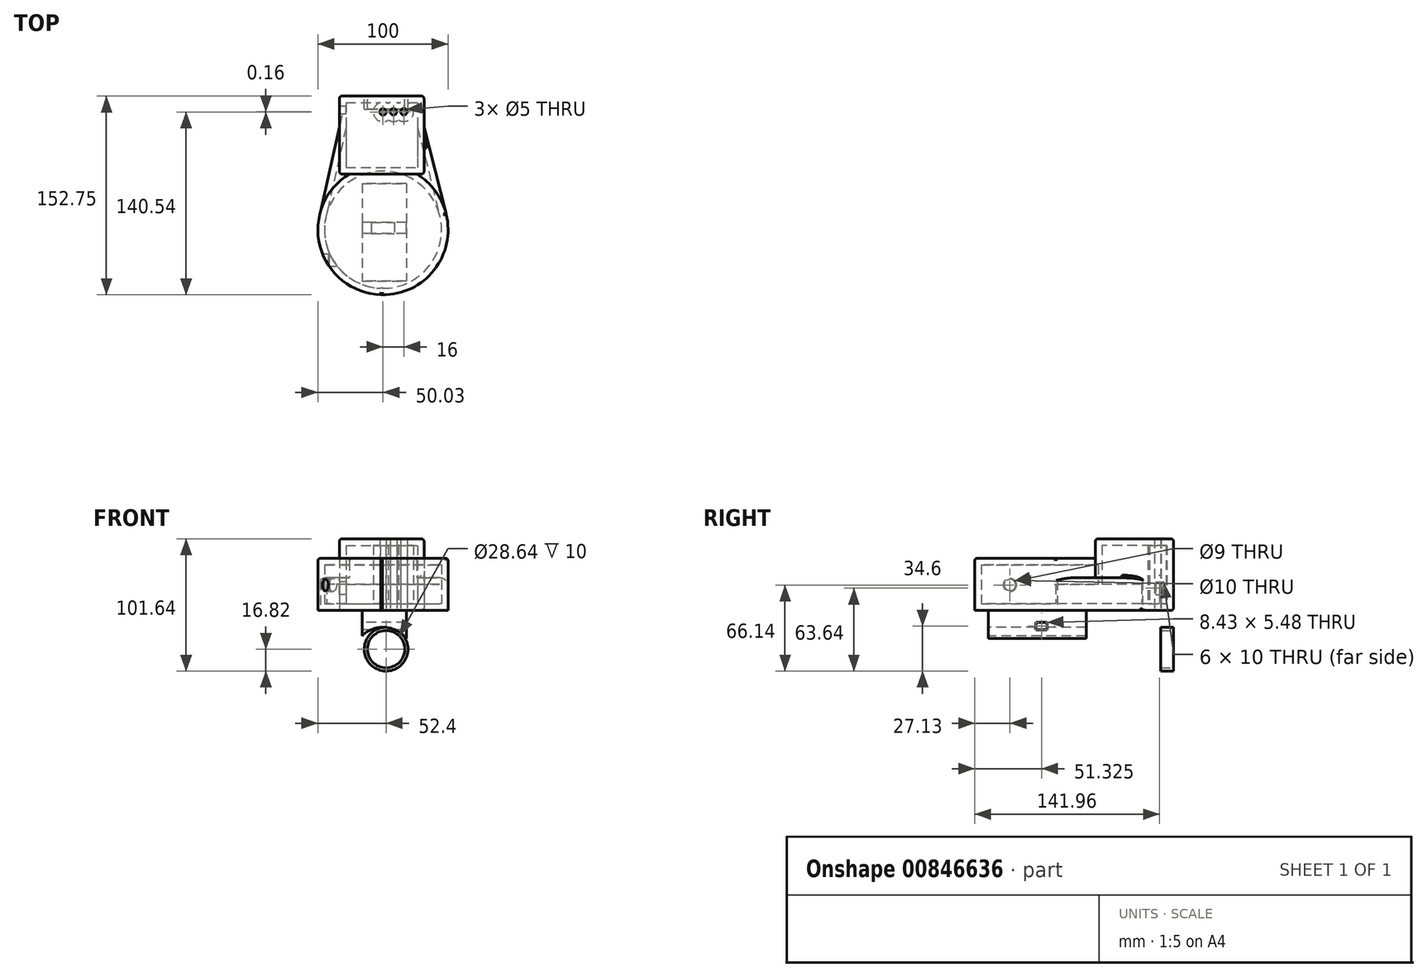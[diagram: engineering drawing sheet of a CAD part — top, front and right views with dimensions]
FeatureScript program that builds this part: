
annotation { "Feature Type Name" : "Feature", "Feature Type Description" : "" }
export const myFeature = defineFeature(function(context is Context, id is Id, definition is map)
    precondition{}
    {
        {
            var Q0;
            Q0=qCreatedBy(makeId("Top.planeOp"),FACE);
            var sketch = newSketch(context, id + "F0", { "sketchPlane" : qUnion([Q0])});
            skLineSegment(sketch, "E0.bottom", {"start": v(-33.47, 67.15) * mm, "end": v(31.53, 67.15) * mm});
            skLineSegment(sketch, "E0.top", {"start": v(-33.47, 7.15) * mm, "end": v(31.53, 7.15) * mm});
            skLineSegment(sketch, "E0.left", {"start": v(-33.47, 67.15) * mm, "end": v(-33.47, 7.15) * mm});
            skLineSegment(sketch, "E0.right", {"start": v(31.53, 67.15) * mm, "end": v(31.53, 7.15) * mm});
            skLineSegment(sketch, "E1.top", {"start": v(-28.47, 32.15) * mm, "end": v(-23.47, 32.15) * mm});
            skLineSegment(sketch, "E1.left", {"start": v(-28.47, 42.15) * mm, "end": v(-28.47, 32.15) * mm});
            skLineSegment(sketch, "E1.right", {"start": v(-23.47, 42.15) * mm, "end": v(-23.47, 32.15) * mm});
            skCircle(sketch, "E2", {"center": v(0, -35.6) * mm, "radius": 50 * mm});
            skLineSegment(sketch, "E3", {"start": v(-28.47, 42.15) * mm, "end": v(-23.47, 42.15) * mm});
            skCircle(sketch, "E4", {"center": v(0.03, 54.94) * mm, "radius": 2.5 * mm});
            skCircle(sketch, "E5", {"center": v(8.03, 55.08) * mm, "radius": 2.5 * mm});
            skCircle(sketch, "E6", {"center": v(16.03, 55.1) * mm, "radius": 2.5 * mm});
            skPoint(sketch, "E7.endSnap0", {"position": v(63.48, -66.15) * mm});
            skPoint(sketch, "E7.start.orphan", {"position": v(90.68, -62.3) * mm});
            skPoint(sketch, "E8.start.orphan", {"position": v(63.48, -90.93) * mm});
            skLineSegment(sketch, "E9", {"start": v(-33.47, 7.15) * mm, "end": v(-33.47, 1.55) * mm});
            skLineSegment(sketch, "E10", {"start": v(31.53, 7.15) * mm, "end": v(32.4, 2.49) * mm});
            skPoint(sketch, "E11.end.orphan", {"position": v(36.27, -70.01) * mm});
            skLineSegment(sketch, "E12", {"start": v(31.53, 43.32) * mm, "end": v(50.78, -32.42) * mm});
            skLineSegment(sketch, "E13", {"start": v(-33.47, 43.32) * mm, "end": v(-48.16, -22.17) * mm});
            skLineSegment(sketch, "E14", {"start": v(46.54, -86.53) * mm, "end": v(-67.67, -84.26) * mm});
            skSolve(sketch);
        }
        {
            var Q0;
            {var subQ1=sQuery(id+"F0.wireOp",EDGE,"E2");var subQ8=makeQuery(id+"F0.imprint","INTERSECT",VERTEX,{"derivedFrom":[subQ1,sQuery(id+"F0.wireOp",EDGE,"E10")]});Q0=makeQuery(id+"F0.imprint","IMPRINT",FACE,{"disambiguationData":[TD([[makeQuery(id+"F0.imprint","IMPRINT",EDGE,{"disambiguationData":[TD([[subQ8,1.0]])],"derivedFrom":subQ1}),1.0]])]});}
            var Q1;
            Q1=sQuery(id+"F0.wireOp",EDGE,"E2");
            extrude(context, id + "F1", {"entities" : qUnion([Q0]), "surfaceEntities" : qUnion([Q1]), "depth" : 40 * mm, "offsetDistance" : 25 * mm});
        }
        {
            var Q0;
            {var subQ0=sQuery(id+"F0.wireOp",EDGE,"E9");Q0=makeQuery(id+"F0.imprint","IMPRINT",FACE,{"disambiguationData":[TD([[makeQuery(id+"F0.imprint","IMPRINT",EDGE,{"derivedFrom":subQ0}),-1.0]])]});}
            var Q1;
            Q1=makeQuery(id+"F0.imprint","IMPRINT",FACE,{"disambiguationData":[TD([[makeQuery(id+"F0.imprint","IMPRINT",EDGE,{"derivedFrom":sQuery(id+"F0.wireOp",EDGE,"E0.top")}),-1.0]])]});
            var Q2;
            {var subQ0=sQuery(id+"F0.wireOp",EDGE,"E10");Q2=makeQuery(id+"F0.imprint","IMPRINT",FACE,{"disambiguationData":[TD([[makeQuery(id+"F0.imprint","IMPRINT",EDGE,{"derivedFrom":subQ0}),1.0]])]});}
            extrude(context, id + "F2", {"entities" : qUnion([Q0, Q1, Q2]), "operationType" : NewBodyOperationType.ADD, "depth" : 25 * mm, "offsetDistance" : 25 * mm});
        }
        {
            var Q0;
            Q0=makeQuery(id+"F0.imprint","IMPRINT",FACE,{"disambiguationData":[TD([[makeQuery(id+"F0.imprint","IMPRINT",EDGE,{"derivedFrom":sQuery(id+"F0.wireOp",EDGE,"E1.top")}),1.0]])]});
            var Q1;
            {var subQ3=sQuery(id+"F0.wireOp",EDGE,"E0.bottom");Q1=makeQuery(id+"F0.imprint","IMPRINT",FACE,{"disambiguationData":[TD([[makeQuery(id+"F0.imprint","IMPRINT",EDGE,{"derivedFrom":subQ3}),-1.0]])]});}
            var Q2;
            Q2=makeQuery(id+"F0.imprint","IMPRINT",FACE,{"disambiguationData":[TD([[makeQuery(id+"F0.imprint","IMPRINT",EDGE,{"derivedFrom":sQuery(id+"F0.wireOp",EDGE,"E4")}),1.0]])]});
            var Q3;
            Q3=makeQuery(id+"F0.imprint","IMPRINT",FACE,{"disambiguationData":[TD([[makeQuery(id+"F0.imprint","IMPRINT",EDGE,{"derivedFrom":sQuery(id+"F0.wireOp",EDGE,"E5")}),1.0]])]});
            var Q4;
            Q4=makeQuery(id+"F0.imprint","IMPRINT",FACE,{"disambiguationData":[TD([[makeQuery(id+"F0.imprint","IMPRINT",EDGE,{"derivedFrom":sQuery(id+"F0.wireOp",EDGE,"E6")}),1.0]])]});
            var Q5;
            {var subQ0=sQuery(id+"F0.wireOp",EDGE,"E2");var subQ1=sQuery(id+"F0.wireOp",EDGE,"E0.top");var subQ2=makeQuery(id+"F0.imprint","INTERSECT",VERTEX,{"disambiguationData":[OD(0.0)],"derivedFrom":[subQ1,subQ0]});Q5=makeQuery(id+"F0.imprint","IMPRINT",FACE,{"disambiguationData":[TD([[makeQuery(id+"F0.imprint","IMPRINT",EDGE,{"disambiguationData":[TD([[subQ2,-1.0]])],"derivedFrom":subQ1}),1.0]])]});}
            extrude(context, id + "F3", {"entities" : qUnion([Q0, Q1, Q2, Q3, Q4, Q5]), "operationType" : NewBodyOperationType.ADD, "surfaceOperationType" : NewSurfaceOperationType.ADD, "depth" : 55 * mm, "offsetDistance" : 25 * mm});
        }
        {
            var Q0;
            Q0=makeQuery(id+"F3.opExtrude","SWEPT_FACE",FACE,{"disambiguationData":[OSD([sQuery(id+"F0.wireOp",EDGE,"E0.bottom")])]});
            var sketch = newSketch(context, id + "F4", { "sketchPlane" : qUnion([Q0])});
            skCircle(sketch, "E15", {"center": v(-2.4, -29.82) * mm, "radius": 14.32 * mm});
            skCircle(sketch, "E16", {"center": v(-2.4, -29.82) * mm, "radius": 16.82 * mm});
            skLineSegment(sketch, "E17", {"start": v(-9.01, 0) * mm, "end": v(-9.01, -14.35) * mm});
            skLineSegment(sketch, "E18", {"start": v(4.98, 0) * mm, "end": v(4.98, -14.7) * mm});
            skSolve(sketch);
        }
        {
            var Q0;
            Q0=sQuery(id+"F0.wireOp",VERTEX,"E4.center");
            var Q1;
            Q1=sQuery(id+"F0.wireOp",VERTEX,"E5.center");
            var Q2;
            Q2=sQuery(id+"F0.wireOp",VERTEX,"E6.center");
            var Q3;
            Q3=makeQuery(id+"F1.opExtrude","SWEPT_BODY",BODY,{"disambiguationData":[OSD([sQuery(id+"F0.wireOp",EDGE,"E2"),sQuery(id+"F0.wireOp",EDGE,"5vXzBK3q-LOnD-Q0HQ-j5aD-O0o9f5yey0at"),sQuery(id+"F0.wireOp",EDGE,"E11")])]});
            hole(context, id + "F5", {"style" : HoleStyle.SIMPLE, "endStyle" : HoleEndStyle.THROUGH, "oppositeDirection" : true, "holeDiameter" : 5 * mm, "majorDiameter" : 5 * mm, "isTappedThrough" : true, "tappedDepth" : 12 * mm, "tapClearance" : 3, "locations" : qUnion([Q0, Q1, Q2]), "scope" : qUnion([Q3])});
        }
        {
            var Q0;
            Q0=makeQuery(id+"F3.opExtrude","SWEPT_FACE",FACE,{"disambiguationData":[OSD([sQuery(id+"F0.wireOp",EDGE,"E0.left")])]});
            var sketch = newSketch(context, id + "F6", { "sketchPlane" : qUnion([Q0])});
            skLineSegment(sketch, "E19.bottom", {"start": v(-59.36, 12) * mm, "end": v(-53.36, 12) * mm});
            skLineSegment(sketch, "E19.top", {"start": v(-59.36, 22) * mm, "end": v(-53.36, 22) * mm});
            skLineSegment(sketch, "E19.left", {"start": v(-59.36, 12) * mm, "end": v(-59.36, 22) * mm});
            skLineSegment(sketch, "E19.right", {"start": v(-53.36, 12) * mm, "end": v(-53.36, 22) * mm});
            skCircle(sketch, "E20", {"center": v(58.47, 19.5) * mm, "radius": 4.5 * mm});
            skSolve(sketch);
        }
        {
            var Q0;
            {var subQ0=sQuery(id+"F4.wireOp",EDGE,"E17");Q0=makeQuery(id+"F4.imprint","IMPRINT",FACE,{"disambiguationData":[TD([[makeQuery(id+"F4.imprint","IMPRINT",EDGE,{"derivedFrom":subQ0}),1.0]])]});}
            var Q1;
            Q1=makeQuery(id+"F4.imprint","IMPRINT",FACE,{"disambiguationData":[TD([[makeQuery(id+"F4.imprint","IMPRINT",EDGE,{"derivedFrom":sQuery(id+"F4.wireOp",EDGE,"E15")}),-1.0]])]});
            extrude(context, id + "F7", {"entities" : qUnion([Q0, Q1]), "operationType" : NewBodyOperationType.ADD, "oppositeDirection" : true, "depth" : 10 * mm, "offsetDistance" : 25 * mm});
        }
        {
            var Q0;
            Q0=makeQuery(id+"F1.opExtrude","SWEPT_FACE",FACE,{"disambiguationData":[OSD([sQuery(id+"F0.wireOp",EDGE,"E2")])]});
            var Q1;
            Q1=makeQuery(id+"F2.opExtrude","SWEPT_FACE",FACE,{"disambiguationData":[OSD([sQuery(id+"F0.wireOp",EDGE,"E12")])]});
            var Q2;
            {var subQ0=sQuery(id+"F0.wireOp",EDGE,"E0.right");var subQ1=sQuery(id+"F0.wireOp",EDGE,"E0.left");var subQ2=sQuery(id+"F0.wireOp",EDGE,"E0.top");var subQ3=sQuery(id+"F0.wireOp",EDGE,"E2");Q2=makeQuery(id+"F3.boolean.opBoolean","MERGE",FACE,{"derivedFrom":[makeQuery(id+"F2.boolean.opBoolean","MERGE",FACE,{"derivedFrom":[makeQuery(id+"F1.opExtrude","CAP_FACE",FACE,{"disambiguationData":[OSD([subQ2,subQ3])],"isStart":true}),makeQuery(id+"F2.opExtrude","CAP_FACE",FACE,{"disambiguationData":[OSD([subQ2,subQ1,subQ3,sQuery(id+"F0.wireOp",EDGE,"E13")])],"isStart":true}),makeQuery(id+"F2.opExtrude","CAP_FACE",FACE,{"disambiguationData":[OSD([subQ2,subQ0,subQ3,sQuery(id+"F0.wireOp",EDGE,"E12")])],"isStart":true})]}),makeQuery(id+"F3.opExtrude","CAP_FACE",FACE,{"disambiguationData":[OSD([sQuery(id+"F0.wireOp",EDGE,"E0.bottom"),subQ2,subQ1,subQ0])],"isStart":true})]});}
            var Q3;
            Q3=makeQuery(id+"F3.opExtrude","SWEPT_FACE",FACE,{"disambiguationData":[OSD([sQuery(id+"F0.wireOp",EDGE,"E0.right")])]});
            var Q4;
            Q4=makeQuery(id+"F3.opExtrude","SWEPT_FACE",FACE,{"disambiguationData":[OSD([sQuery(id+"F0.wireOp",EDGE,"E0.left")])]});
            var Q5;
            Q5=makeQuery(id+"F3.opExtrude","CAP_FACE",FACE,{"disambiguationData":[OSD([sQuery(id+"F0.wireOp",EDGE,"E0.bottom"),sQuery(id+"F0.wireOp",EDGE,"E0.top"),sQuery(id+"F0.wireOp",EDGE,"E0.left"),sQuery(id+"F0.wireOp",EDGE,"E0.right")])],"isStart":false});
            var Q6;
            Q6=makeQuery(id+"F3.opExtrude","SWEPT_FACE",FACE,{"disambiguationData":[OSD([sQuery(id+"F0.wireOp",EDGE,"E0.top")])]});
            var Q7;
            Q7=makeQuery(id+"F2.opExtrude","CAP_FACE",FACE,{"disambiguationData":[OSD([sQuery(id+"F0.wireOp",EDGE,"E0.top"),sQuery(id+"F0.wireOp",EDGE,"E0.left"),sQuery(id+"F0.wireOp",EDGE,"E2"),sQuery(id+"F0.wireOp",EDGE,"E13")])],"isStart":false});
            var Q8;
            Q8=makeQuery(id+"F1.opExtrude","SWEPT_BODY",BODY,{"disambiguationData":[OSD([sQuery(id+"F0.wireOp",EDGE,"E0.top"),sQuery(id+"F0.wireOp",EDGE,"E2")])]});
            shell(context, id + "F8", {"isHollow" : true, "entities" : qUnion([Q0, Q1, Q2, Q3, Q4, Q5, Q6, Q7]), "parts" : qUnion([Q8]), "thickness" : 5 * mm});
        }
        {
            var Q0;
            Q0=sQuery(id+"F6.wireOp",VERTEX,"E20.center");
            var Q1;
            Q1=makeQuery(id+"F1.opExtrude","SWEPT_BODY",BODY,{"disambiguationData":[OSD([sQuery(id+"F0.wireOp",EDGE,"E0.top"),sQuery(id+"F0.wireOp",EDGE,"E2")])]});
            hole(context, id + "F9", {"style" : HoleStyle.C_SINK, "endStyle" : HoleEndStyle.BLIND, "oppositeDirection" : true, "holeDiameter" : 9 * mm, "cSinkDiameter" : 10 * mm, "cSinkAngle" : 90 * degree, "majorDiameter" : 5 * mm, "holeDepth" : 10 * mm, "isTappedThrough" : true, "tappedDepth" : 12 * mm, "tapClearance" : 3, "locations" : qUnion([Q0]), "scope" : qUnion([Q1])});
        }
        {
            var Q0;
            Q0 = qSketchRegion(id + "F6", true);
            extrude(context, id + "F10", {"entities" : qUnion([Q0]), "operationType" : NewBodyOperationType.REMOVE, "oppositeDirection" : true, "depth" : 25 * mm, "offsetDistance" : 25 * mm});
        }
        {
            var Q0;
            Q0=makeQuery(id+"F1.opExtrude","CAP_EDGE",EDGE,{"disambiguationData":[OSD([sQuery(id+"F0.wireOp",EDGE,"E2")])],"isStart":false});
            var Q1;
            Q1=makeQuery(id+"F2.opExtrude","CAP_EDGE",EDGE,{"disambiguationData":[OSD([sQuery(id+"F0.wireOp",EDGE,"E13")])],"isStart":false});
            var Q2;
            Q2=makeQuery(id+"F2.opExtrude","CAP_EDGE",EDGE,{"disambiguationData":[OSD([sQuery(id+"F0.wireOp",EDGE,"E12")])],"isStart":false});
            var Q3;
            Q3=makeQuery(id+"F3.opExtrude","SWEPT_FACE",FACE,{"disambiguationData":[OSD([sQuery(id+"F0.wireOp",EDGE,"E0.right")])]});
            var Q4;
            Q4=makeQuery(id+"F3.opExtrude","CAP_EDGE",EDGE,{"disambiguationData":[OSD([sQuery(id+"F0.wireOp",EDGE,"E0.left")])],"isStart":false});
            var Q5;
            Q5=makeQuery(id+"F3.opExtrude","CAP_EDGE",EDGE,{"disambiguationData":[OSD([sQuery(id+"F0.wireOp",EDGE,"E0.top")])],"isStart":false});
            var Q6;
            {var subQ0=sQuery(id+"F0.wireOp",EDGE,"E0.bottom");var subQ4=sQuery(id+"F0.wireOp",EDGE,"E0.left");Q6=makeQuery(id+"F7.boolean.opBoolean","SPLIT",EDGE,{"disambiguationData":[TD([makeQuery(id+"F3.opExtrude","SWEPT_FACE",FACE,{"disambiguationData":[OSD([subQ4])]})])],"derivedFrom":makeQuery(id+"F3.opExtrude","CAP_EDGE",EDGE,{"disambiguationData":[OSD([subQ0])],"isStart":true})});}
            var Q7;
            {var subQ0=sQuery(id+"F0.wireOp",EDGE,"E0.bottom");var subQ3=sQuery(id+"F0.wireOp",EDGE,"E0.right");Q7=makeQuery(id+"F7.boolean.opBoolean","SPLIT",EDGE,{"disambiguationData":[TD([makeQuery(id+"F3.opExtrude","SWEPT_FACE",FACE,{"disambiguationData":[OSD([subQ3])]})])],"derivedFrom":makeQuery(id+"F3.opExtrude","CAP_EDGE",EDGE,{"disambiguationData":[OSD([subQ0])],"isStart":true})});}
            var Q8;
            Q8=makeQuery(id+"F3.opExtrude","CAP_EDGE",EDGE,{"disambiguationData":[OSD([sQuery(id+"F0.wireOp",EDGE,"E0.bottom")])],"isStart":false});
            var Q9;
            Q9=makeQuery(id+"F3.opExtrude","SWEPT_EDGE",EDGE,{"disambiguationData":[OSD([sQuery(id+"F0.wireOp",EDGE,"E0.bottom"),sQuery(id+"F0.wireOp",EDGE,"E0.left")])]});
            fillet(context, id + "F11", {"entities" : qUnion([Q0, Q1, Q2, Q3, Q4, Q5, Q6, Q7, Q8, Q9]), "radius" : 2 * mm, "tangentPropagation" : true, "allowEdgeOverflow" : false});
        }
        {
            var Q0;
            Q0=makeQuery(id+"F3.opExtrude","SWEPT_EDGE",EDGE,{"disambiguationData":[OSD([sQuery(id+"F0.wireOp",EDGE,"E0.top"),sQuery(id+"F0.wireOp",EDGE,"E0.left"),sQuery(id+"F0.wireOp",EDGE,"E9")])]});
            var Q1;
            Q1=makeQuery(id+"F2.opExtrude","CAP_EDGE",EDGE,{"disambiguationData":[OSD([sQuery(id+"F0.wireOp",EDGE,"E0.left")])],"isStart":false});
            fillet(context, id + "F12", {"entities" : qUnion([Q0, Q1]), "radius" : 2 * mm, "tangentPropagation" : true, "allowEdgeOverflow" : false});
        }
        {
            var Q0;
            Q0=makeQuery(id+"F3.opExtrude","CAP_EDGE",EDGE,{"disambiguationData":[OSD([sQuery(id+"F0.wireOp",EDGE,"E0.left")])],"isStart":true});
            var Q1;
            Q1=makeQuery(id+"F10.boolean.opBoolean","COPY",EDGE,{"derivedFrom":makeQuery(id+"F10.opExtrude","CAP_EDGE",EDGE,{"disambiguationData":[OSD([sQuery(id+"F6.wireOp",EDGE,"E19.top")])],"isStart":true})});
            var Q2;
            Q2=makeQuery(id+"F10.boolean.opBoolean","COPY",EDGE,{"derivedFrom":makeQuery(id+"F10.opExtrude","CAP_EDGE",EDGE,{"disambiguationData":[OSD([sQuery(id+"F6.wireOp",EDGE,"E19.right")])],"isStart":true})});
            var Q3;
            Q3=makeQuery(id+"F10.boolean.opBoolean","COPY",EDGE,{"derivedFrom":makeQuery(id+"F10.opExtrude","CAP_EDGE",EDGE,{"disambiguationData":[OSD([sQuery(id+"F6.wireOp",EDGE,"E19.bottom")])],"isStart":true})});
            var Q4;
            Q4=makeQuery(id+"F10.boolean.opBoolean","COPY",EDGE,{"derivedFrom":makeQuery(id+"F10.opExtrude","CAP_EDGE",EDGE,{"disambiguationData":[OSD([sQuery(id+"F6.wireOp",EDGE,"E19.top")])],"isStart":false})});
            fillet(context, id + "F13", {"entities" : qUnion([Q0, Q1, Q2, Q3, Q4]), "radius" : 2 * mm, "tangentPropagation" : true, "allowEdgeOverflow" : false});
        }
        {
            var Q0;
            {var subQ0=sQuery(id+"F0.wireOp",EDGE,"E2");var subQ2=sQuery(id+"F0.wireOp",EDGE,"E0.top");var subQ3=makeQuery(id+"F0.imprint","INTERSECT",VERTEX,{"disambiguationData":[OD(0.0)],"derivedFrom":[subQ2,subQ0]});Q0=makeQuery(id+"F0.imprint","IMPRINT",FACE,{"disambiguationData":[TD([[makeQuery(id+"F0.imprint","IMPRINT",EDGE,{"disambiguationData":[TD([[subQ3,-1.0]])],"derivedFrom":subQ2}),-1.0]])]});}
            var sketch = newSketch(context, id + "F14", { "sketchPlane" : qUnion([Q0])});
            skLineSegment(sketch, "E21.bottom", {"start": v(-16.14, -75) * mm, "end": v(17.86, -75) * mm});
            skLineSegment(sketch, "E21.top", {"start": v(-16.14, 0) * mm, "end": v(17.86, 0) * mm});
            skLineSegment(sketch, "E21.left", {"start": v(-16.14, -75) * mm, "end": v(-16.14, 0) * mm});
            skLineSegment(sketch, "E21.right", {"start": v(17.86, -75) * mm, "end": v(17.86, 0) * mm});
            skSolve(sketch);
        }
        {
            var Q0;
            Q0=makeQuery(id+"F14.imprint","IMPRINT",FACE,{"disambiguationData":[TD([[makeQuery(id+"F14.imprint","IMPRINT",EDGE,{"derivedFrom":sQuery(id+"F14.wireOp",EDGE,"E21.bottom")}),1.0]])]});
            var Q1;
            Q1=sQuery(id+"F14.wireOp",EDGE,"E21.left");
            var Q2;
            Q2=sQuery(id+"F14.wireOp",EDGE,"E21.right");
            var Q3;
            Q3=sQuery(id+"F14.wireOp",EDGE,"E21.bottom");
            var Q4;
            Q4=sQuery(id+"F14.wireOp",EDGE,"E21.top");
            extrude(context, id + "F15", {"entities" : qUnion([Q0]), "operationType" : NewBodyOperationType.ADD, "surfaceEntities" : qUnion([Q1, Q2, Q3, Q4]), "oppositeDirection" : true, "depth" : 30 * mm, "offsetDistance" : 25 * mm});
        }
        {
            var Q0;
            Q0=makeQuery(id+"F15.opExtrude","SWEPT_FACE",FACE,{"disambiguationData":[OSD([sQuery(id+"F14.wireOp",EDGE,"E21.bottom")])]});
            var sketch = newSketch(context, id + "F16", { "sketchPlane" : qUnion([Q0])});
            skPoint(sketch, "E22.center.orphan", {"position": v(0, -30) * mm});
            skCircle(sketch, "E23", {"center": v(0, -36) * mm, "radius": 23.2 * mm});
            skCircle(sketch, "E24", {"center": v(0, -36) * mm, "radius": 23 * mm});
            skSolve(sketch);
        }
        {
            var Q0;
            {var subQ1=sQuery(id+"F14.wireOp",EDGE,"E21.bottom");var subQ6=makeQuery(id+"F15.opExtrude","CAP_EDGE",EDGE,{"disambiguationData":[OSD([subQ1])],"isStart":false});Q0=makeQuery(id+"F16.imprint","IMPRINT",FACE,{"disambiguationData":[TD([[makeQuery(id+"F16.imprint","IMPRINT",EDGE,{"derivedFrom":subQ6}),1.0]])]});}
            extrude(context, id + "F17", {"entities" : qUnion([Q0]), "operationType" : NewBodyOperationType.REMOVE, "oppositeDirection" : true, "depth" : 100 * mm, "offsetDistance" : 25 * mm});
        }
        {
            var Q0;
            Q0=makeQuery(id+"F15.opExtrude","SWEPT_FACE",FACE,{"disambiguationData":[OSD([sQuery(id+"F14.wireOp",EDGE,"E21.left")])]});
            var sketch = newSketch(context, id + "F18", { "sketchPlane" : qUnion([Q0])});
            skLineSegment(sketch, "E25.bottom", {"start": v(30.06, -9.3) * mm, "end": v(38.49, -9.3) * mm});
            skLineSegment(sketch, "E25.top", {"start": v(30.06, -14.78) * mm, "end": v(38.49, -14.78) * mm});
            skLineSegment(sketch, "E25.left", {"start": v(30.06, -9.3) * mm, "end": v(30.06, -14.78) * mm});
            skLineSegment(sketch, "E25.right", {"start": v(38.49, -9.3) * mm, "end": v(38.49, -14.78) * mm});
            skSolve(sketch);
        }
        {
            var Q0;
            Q0=makeQuery(id+"F18.imprint","IMPRINT",FACE,{"disambiguationData":[TD([[makeQuery(id+"F18.imprint","IMPRINT",EDGE,{"derivedFrom":sQuery(id+"F18.wireOp",EDGE,"E25.bottom")}),-1.0]])]});
            extrude(context, id + "F19", {"entities" : qUnion([Q0]), "operationType" : NewBodyOperationType.REMOVE, "oppositeDirection" : true, "depth" : 50 * mm, "offsetDistance" : 25 * mm});
        }
    });
